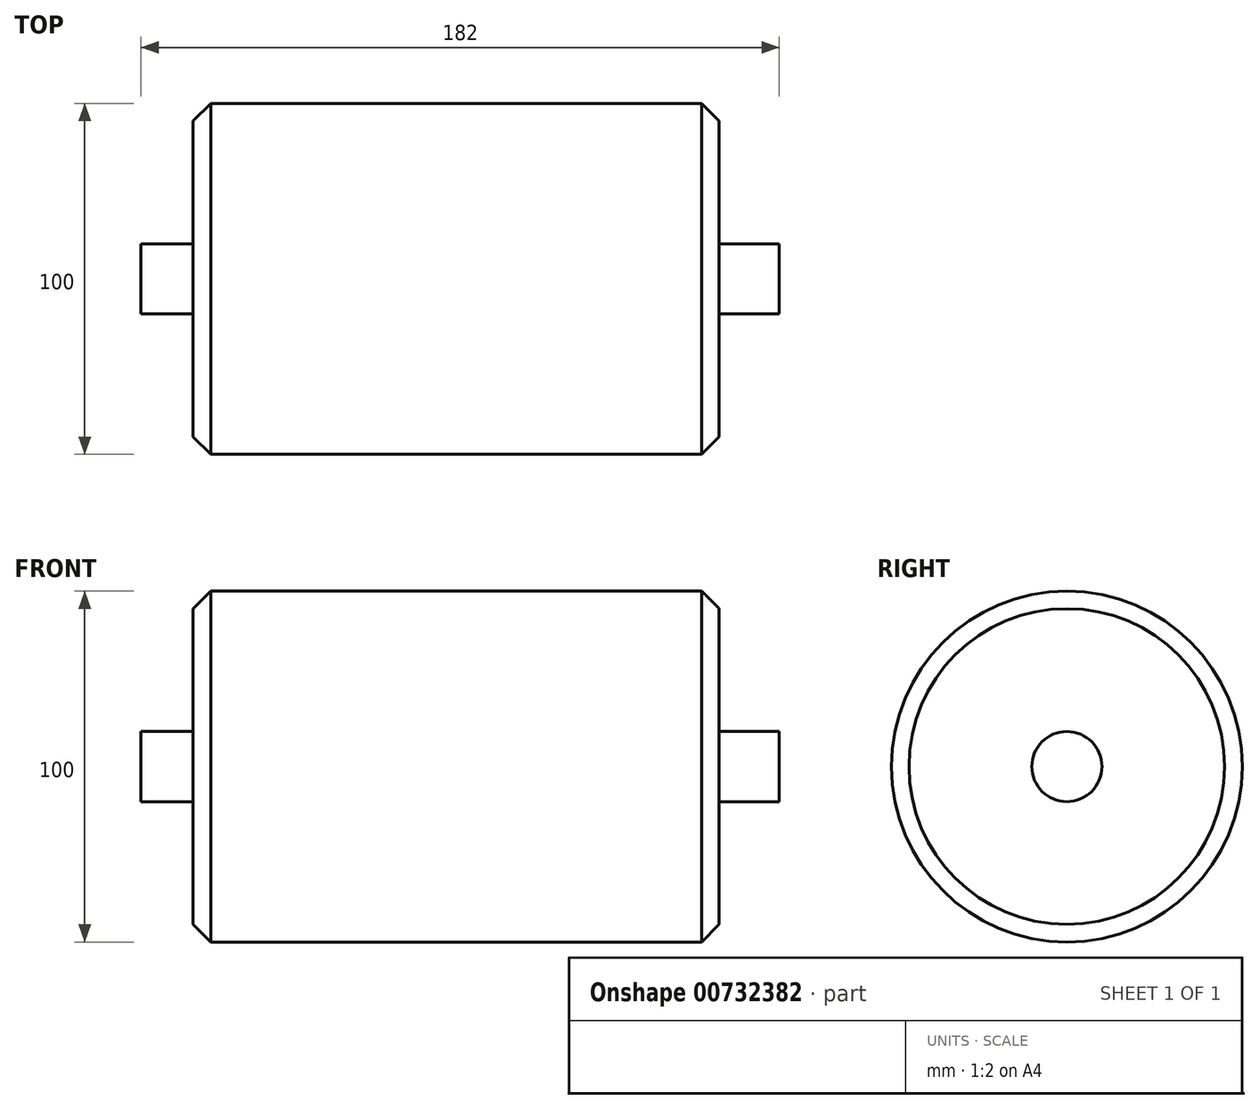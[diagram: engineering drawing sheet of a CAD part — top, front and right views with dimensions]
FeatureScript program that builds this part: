
annotation { "Feature Type Name" : "Feature", "Feature Type Description" : "" }
export const myFeature = defineFeature(function(context is Context, id is Id, definition is map)
    precondition{}
    {
        {
            var Q0;
            Q0=qCreatedBy(makeId("Front.planeOp"),FACE);
            var sketch = newSketch(context, id + "F0", { "sketchPlane" : qUnion([Q0])});
            skLineSegment(sketch, "E0", {"start": v(-102.4, 0) * mm, "end": v(-102.4, 10) * mm});
            skLineSegment(sketch, "E1", {"start": v(-102.4, 10) * mm, "end": v(-87.54, 10) * mm});
            skLineSegment(sketch, "E2", {"start": v(-87.54, 10) * mm, "end": v(-87.54, 50) * mm});
            skLineSegment(sketch, "E3", {"start": v(-87.54, 50) * mm, "end": v(62.46, 50) * mm});
            skLineSegment(sketch, "E4", {"start": v(62.46, 50) * mm, "end": v(62.46, 10) * mm});
            skLineSegment(sketch, "E5", {"start": v(62.46, 10) * mm, "end": v(79.6, 10) * mm});
            skLineSegment(sketch, "E6", {"start": v(79.6, 10) * mm, "end": v(79.6, 0) * mm});
            skLineSegment(sketch, "E7", {"start": v(79.6, 0) * mm, "end": v(-102.4, 0) * mm});
            skSolve(sketch);
        }
        {
            var Q0;
            Q0=makeQuery(id+"F0.imprint","IMPRINT",FACE,{"disambiguationData":[TD([[makeQuery(id+"F0.imprint","IMPRINT",EDGE,{"derivedFrom":sQuery(id+"F0.wireOp",EDGE,"E0")}),-1.0]])]});
            var Q1;
            Q1=sQuery(id+"F0.wireOp",EDGE,"E7");
            revolve(context, id + "F1", {"surfaceOperationType" : NewSurfaceOperationType.NEW, "entities" : qUnion([Q0]), "axis" : qUnion([Q1]), "revolveType" : RevolveType.FULL});
        }
        {
            var Q0;
            Q0=makeQuery(id+"F1.opRevolve","SWEPT_EDGE",EDGE,{"disambiguationData":[OSD([sQuery(id+"F0.wireOp",EDGE,"E2"),sQuery(id+"F0.wireOp",EDGE,"E3")])]});
            var Q1;
            Q1=makeQuery(id+"F1.opRevolve","SWEPT_EDGE",EDGE,{"disambiguationData":[OSD([sQuery(id+"F0.wireOp",EDGE,"E3"),sQuery(id+"F0.wireOp",EDGE,"E4")])]});
            chamfer(context, id + "F2", {"entities" : qUnion([Q0, Q1]), "width" : 5 * mm, "tangentPropagation" : true});
        }
    });
